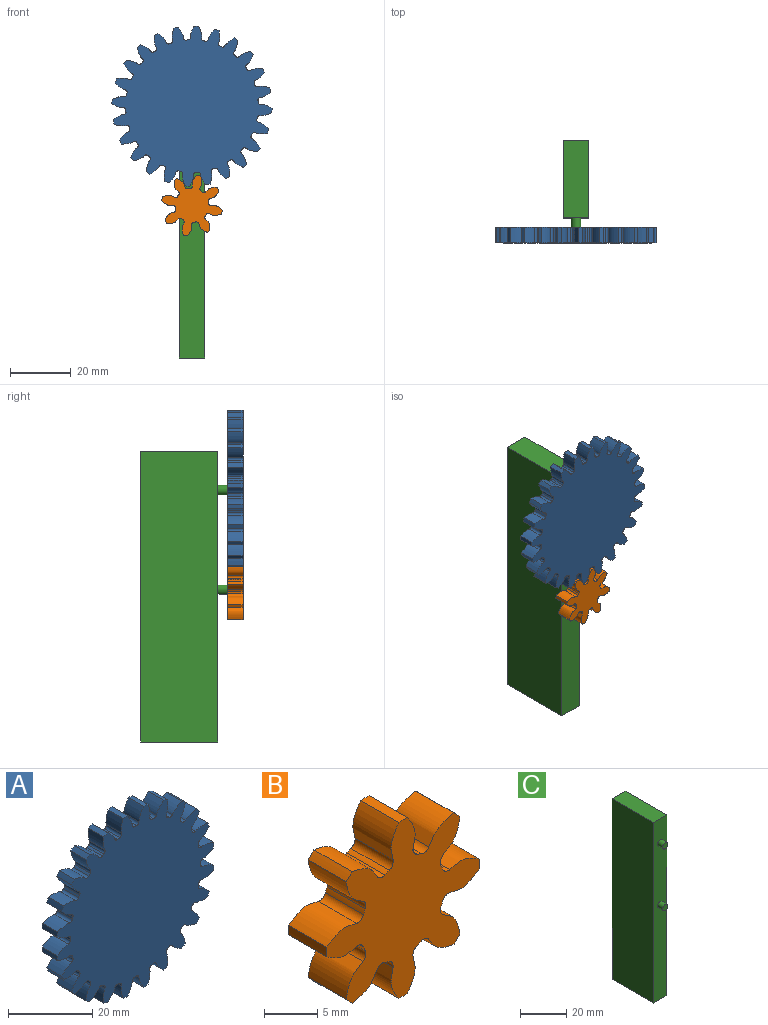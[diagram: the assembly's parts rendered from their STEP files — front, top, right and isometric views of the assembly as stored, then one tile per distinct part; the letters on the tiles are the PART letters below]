
ASSEMBLY  parts=3 mates=2
PART A: 146 faces, bbox 52.6x5.1x52.6 mm
  f0: cylinder r=26.42mm len=5.08mm, axis (0,1,0), area 7.4mm2, adj f23,f25,f121,f143
  f1: cylinder r=26.42mm len=5.08mm, axis (0,1,0), area 7.4mm2, adj f23,f25,f138,f141
  f2: cylinder r=26.42mm len=5.08mm, axis (0,1,0), area 7.4mm2, adj f23,f25,f126,f133
  f3: cylinder r=26.42mm len=5.08mm, axis (0,1,0), area 7.4mm2, adj f23,f25,f128,f136
  f4: cylinder r=26.42mm len=5.08mm, axis (0,1,0), area 7.4mm2, adj f23,f25,f116,f123
  f5: cylinder r=26.42mm len=5.08mm, axis (0,1,0), area 7.4mm2, adj f23,f25,f106,f118
  f6: cylinder r=26.42mm len=5.08mm, axis (0,1,0), area 7.4mm2, adj f23,f25,f101,f113
  f7: cylinder r=26.42mm len=5.08mm, axis (0,1,0), area 7.4mm2, adj f23,f25,f108,f111
  f8: cylinder r=26.42mm len=5.08mm, axis (0,1,0), area 7.4mm2, adj f23,f25,f96,f103
  f9: cylinder r=26.42mm len=5.08mm, axis (0,1,0), area 7.4mm2, adj f23,f25,f91,f98
  f10: cylinder r=26.42mm len=5.08mm, axis (0,1,0), area 7.4mm2, adj f23,f25,f86,f93
  f11: cylinder r=26.42mm len=5.08mm, axis (0,1,0), area 7.4mm2, adj f23,f25,f71,f88
  f12: cylinder r=26.42mm len=5.08mm, axis (0,1,0), area 7.4mm2, adj f23,f25,f26,f83
  f13: cylinder r=26.42mm len=5.08mm, axis (0,1,0), area 7.4mm2, adj f23,f25,f78,f81
  f14: cylinder r=26.42mm len=5.08mm, axis (0,1,0), area 7.4mm2, adj f23,f25,f66,f73
  f15: cylinder r=26.42mm len=5.08mm, axis (0,1,0), area 7.4mm2, adj f23,f25,f68,f76
  f16: cylinder r=26.42mm len=5.08mm, axis (0,1,0), area 7.4mm2, adj f23,f25,f51,f63
  f17: cylinder r=26.42mm len=5.08mm, axis (0,1,0), area 7.4mm2, adj f23,f25,f46,f58
  f18: cylinder r=26.42mm len=5.08mm, axis (0,1,0), area 7.4mm2, adj f23,f25,f53,f56
  f19: cylinder r=26.42mm len=5.08mm, axis (0,1,0), area 7.4mm2, adj f23,f25,f41,f48
  f20: cylinder r=26.42mm len=5.08mm, axis (0,1,0), area 7.4mm2, adj f23,f25,f36,f43
  f21: cylinder r=26.42mm len=5.08mm, axis (0,1,0), area 7.4mm2, adj f23,f25,f31,f38
  f22: cylinder r=26.42mm len=5.08mm, axis (0,1,0), area 7.4mm2, adj f23,f25,f33,f131
  f23: plane 52.56x52.56mm, normal (0,-1,0), area 1838.6mm2, adj f0,f1,f2,f3,f4,f5,f6,f7
  f24: cylinder r=26.42mm len=5.08mm, axis (0,1,0), area 7.4mm2, adj f23,f25,f28,f61
  f25: plane 52.56x52.56mm, normal (0,1,0), area 1838.6mm2, adj f0,f1,f2,f3,f4,f5,f6,f7
  f26: extruded ~5.08x3.7mm, area 20.7mm2, adj f12,f23,f25,f29
  f27: cylinder r=21.84mm len=5.08mm, axis (0,1,0), area 3.6mm2, adj f23,f25,f29,f30
  f28: extruded ~5.08x3.7mm, area 20.7mm2, adj f23,f24,f25,f30
  f29: cylinder r=0.78mm len=5.08mm, axis (0,1,0), area 6.1mm2, adj f23,f25,f26,f27
  f30: cylinder r=0.78mm len=5.08mm, axis (0,1,0), area 6.1mm2, adj f23,f25,f27,f28
  f31: extruded ~5.08x3.98mm, area 20.7mm2, adj f21,f23,f25,f34
  f32: cylinder r=21.84mm len=5.08mm, axis (0,1,0), area 3.6mm2, adj f23,f25,f34,f35
  f33: extruded ~5.08x3.16mm, area 20.7mm2, adj f22,f23,f25,f35
  f34: cylinder r=0.78mm len=5.08mm, axis (0,1,0), area 6.1mm2, adj f23,f25,f31,f32
  f35: cylinder r=0.78mm len=5.08mm, axis (0,1,0), area 6.1mm2, adj f23,f25,f32,f33
  f36: extruded ~5.08x3.7mm, area 20.7mm2, adj f20,f23,f25,f39
  f37: cylinder r=21.84mm len=5.08mm, axis (0,1,0), area 3.6mm2, adj f23,f25,f39,f40
  f38: extruded ~5.08x3.7mm, area 20.7mm2, adj f21,f23,f25,f40
  f39: cylinder r=0.78mm len=5.08mm, axis (0,1,0), area 6.1mm2, adj f23,f25,f36,f37
  f40: cylinder r=0.78mm len=5.08mm, axis (0,1,0), area 6.1mm2, adj f23,f25,f37,f38
  f41: extruded ~5.08x3.16mm, area 20.7mm2, adj f19,f23,f25,f44
  f42: cylinder r=21.84mm len=5.08mm, axis (0,1,0), area 3.6mm2, adj f23,f25,f44,f45
  f43: extruded ~5.08x3.98mm, area 20.7mm2, adj f20,f23,f25,f45
  f44: cylinder r=0.78mm len=5.08mm, axis (0,1,0), area 6.1mm2, adj f23,f25,f41,f42
  f45: cylinder r=0.78mm len=5.08mm, axis (0,1,0), area 6.1mm2, adj f23,f25,f42,f43
  f46: extruded ~5.08x3.22mm, area 20.7mm2, adj f17,f23,f25,f49
  f47: cylinder r=21.84mm len=5.08mm, axis (0,1,0), area 3.6mm2, adj f23,f25,f49,f50
  f48: extruded ~5.08x4mm, area 20.7mm2, adj f19,f23,f25,f50
  f49: cylinder r=0.78mm len=5.08mm, axis (0,1,0), area 6.1mm2, adj f23,f25,f46,f47
  f50: cylinder r=0.78mm len=5.08mm, axis (0,1,0), area 6.1mm2, adj f23,f25,f47,f48
  f51: extruded ~5.08x4mm, area 20.7mm2, adj f16,f23,f25,f54
  f52: cylinder r=21.84mm len=5.08mm, axis (0,1,0), area 3.6mm2, adj f23,f25,f54,f55
  f53: extruded ~5.08x3.22mm, area 20.7mm2, adj f18,f23,f25,f55
  f54: cylinder r=0.78mm len=5.08mm, axis (0,1,0), area 6.1mm2, adj f23,f25,f51,f52
  f55: cylinder r=0.78mm len=5.08mm, axis (0,1,0), area 6.1mm2, adj f23,f25,f52,f53
  f56: extruded ~5.08x3.74mm, area 20.7mm2, adj f18,f23,f25,f59
  f57: cylinder r=21.84mm len=5.08mm, axis (0,1,0), area 3.6mm2, adj f23,f25,f59,f60
  f58: extruded ~5.08x3.74mm, area 20.7mm2, adj f17,f23,f25,f60
  f59: cylinder r=0.78mm len=5.08mm, axis (0,1,0), area 6.1mm2, adj f23,f25,f56,f57
  f60: cylinder r=0.78mm len=5.08mm, axis (0,1,0), area 6.1mm2, adj f23,f25,f57,f58
  f61: extruded ~5.08x3.98mm, area 20.7mm2, adj f23,f24,f25,f64
  f62: cylinder r=21.84mm len=5.08mm, axis (0,1,0), area 3.6mm2, adj f23,f25,f64,f65
  f63: extruded ~5.08x3.16mm, area 20.7mm2, adj f16,f23,f25,f65
  f64: cylinder r=0.78mm len=5.08mm, axis (0,1,0), area 6.1mm2, adj f23,f25,f61,f62
  f65: cylinder r=0.78mm len=5.08mm, axis (0,1,0), area 6.1mm2, adj f23,f25,f62,f63
  f66: extruded ~5.08x3.74mm, area 20.7mm2, adj f14,f23,f25,f69
  f67: cylinder r=21.84mm len=5.08mm, axis (0,1,0), area 3.6mm2, adj f23,f25,f69,f70
  f68: extruded ~5.08x3.74mm, area 20.7mm2, adj f15,f23,f25,f70
  f69: cylinder r=0.78mm len=5.08mm, axis (0,1,0), area 6.1mm2, adj f23,f25,f66,f67
  f70: cylinder r=0.78mm len=5.08mm, axis (0,1,0), area 6.1mm2, adj f23,f25,f67,f68
  f71: extruded ~5.08x4mm, area 20.7mm2, adj f11,f23,f25,f74
  f72: cylinder r=21.84mm len=5.08mm, axis (0,1,0), area 3.6mm2, adj f23,f25,f74,f75
  f73: extruded ~5.08x3.22mm, area 20.7mm2, adj f14,f23,f25,f75
  f74: cylinder r=0.78mm len=5.08mm, axis (0,1,0), area 6.1mm2, adj f23,f25,f71,f72
  f75: cylinder r=0.78mm len=5.08mm, axis (0,1,0), area 6.1mm2, adj f23,f25,f72,f73
  f76: extruded ~5.08x3.22mm, area 20.7mm2, adj f15,f23,f25,f79
  f77: cylinder r=21.84mm len=5.08mm, axis (0,1,0), area 3.6mm2, adj f23,f25,f79,f80
  f78: extruded ~5.08x4mm, area 20.7mm2, adj f13,f23,f25,f80
  f79: cylinder r=0.78mm len=5.08mm, axis (0,1,0), area 6.1mm2, adj f23,f25,f76,f77
  f80: cylinder r=0.78mm len=5.08mm, axis (0,1,0), area 6.1mm2, adj f23,f25,f77,f78
  f81: extruded ~5.08x3.16mm, area 20.7mm2, adj f13,f23,f25,f84
  f82: cylinder r=21.84mm len=5.08mm, axis (0,1,0), area 3.6mm2, adj f23,f25,f84,f85
  f83: extruded ~5.08x3.98mm, area 20.7mm2, adj f12,f23,f25,f85
  f84: cylinder r=0.78mm len=5.08mm, axis (0,1,0), area 6.1mm2, adj f23,f25,f81,f82
  f85: cylinder r=0.78mm len=5.08mm, axis (0,1,0), area 6.1mm2, adj f23,f25,f82,f83
  f86: extruded ~5.08x3.98mm, area 20.7mm2, adj f10,f23,f25,f89
  f87: cylinder r=21.84mm len=5.08mm, axis (0,1,0), area 3.6mm2, adj f23,f25,f89,f90
  f88: extruded ~5.08x3.16mm, area 20.7mm2, adj f11,f23,f25,f90
  f89: cylinder r=0.78mm len=5.08mm, axis (0,1,0), area 6.1mm2, adj f23,f25,f86,f87
  f90: cylinder r=0.78mm len=5.08mm, axis (0,1,0), area 6.1mm2, adj f23,f25,f87,f88
  f91: extruded ~5.08x3.7mm, area 20.7mm2, adj f9,f23,f25,f94
  f92: cylinder r=21.84mm len=5.08mm, axis (0,1,0), area 3.6mm2, adj f23,f25,f94,f95
  f93: extruded ~5.08x3.7mm, area 20.7mm2, adj f10,f23,f25,f95
  f94: cylinder r=0.78mm len=5.08mm, axis (0,1,0), area 6.1mm2, adj f23,f25,f91,f92
  f95: cylinder r=0.78mm len=5.08mm, axis (0,1,0), area 6.1mm2, adj f23,f25,f92,f93
  f96: extruded ~5.08x3.16mm, area 20.7mm2, adj f8,f23,f25,f99
  f97: cylinder r=21.84mm len=5.08mm, axis (0,1,0), area 3.6mm2, adj f23,f25,f99,f100
  f98: extruded ~5.08x3.98mm, area 20.7mm2, adj f9,f23,f25,f100
  f99: cylinder r=0.78mm len=5.08mm, axis (0,1,0), area 6.1mm2, adj f23,f25,f96,f97
  f100: cylinder r=0.78mm len=5.08mm, axis (0,1,0), area 6.1mm2, adj f23,f25,f97,f98
  f101: extruded ~5.08x3.22mm, area 20.7mm2, adj f6,f23,f25,f104
  f102: cylinder r=21.84mm len=5.08mm, axis (0,1,0), area 3.6mm2, adj f23,f25,f104,f105
  f103: extruded ~5.08x4mm, area 20.7mm2, adj f8,f23,f25,f105
  f104: cylinder r=0.78mm len=5.08mm, axis (0,1,0), area 6.1mm2, adj f23,f25,f101,f102
  f105: cylinder r=0.78mm len=5.08mm, axis (0,1,0), area 6.1mm2, adj f23,f25,f102,f103
  f106: extruded ~5.08x4mm, area 20.7mm2, adj f5,f23,f25,f109
  f107: cylinder r=21.84mm len=5.08mm, axis (0,1,0), area 3.6mm2, adj f23,f25,f109,f110
  f108: extruded ~5.08x3.22mm, area 20.7mm2, adj f7,f23,f25,f110
  f109: cylinder r=0.78mm len=5.08mm, axis (0,1,0), area 6.1mm2, adj f23,f25,f106,f107
  f110: cylinder r=0.78mm len=5.08mm, axis (0,1,0), area 6.1mm2, adj f23,f25,f107,f108
  f111: extruded ~5.08x3.74mm, area 20.7mm2, adj f7,f23,f25,f114
  f112: cylinder r=21.84mm len=5.08mm, axis (0,1,0), area 3.6mm2, adj f23,f25,f114,f115
  f113: extruded ~5.08x3.74mm, area 20.7mm2, adj f6,f23,f25,f115
  f114: cylinder r=0.78mm len=5.08mm, axis (0,1,0), area 6.1mm2, adj f23,f25,f111,f112
  f115: cylinder r=0.78mm len=5.08mm, axis (0,1,0), area 6.1mm2, adj f23,f25,f112,f113
  f116: extruded ~5.08x3.98mm, area 20.7mm2, adj f4,f23,f25,f119
  f117: cylinder r=21.84mm len=5.08mm, axis (0,1,0), area 3.6mm2, adj f23,f25,f119,f120
  f118: extruded ~5.08x3.16mm, area 20.7mm2, adj f5,f23,f25,f120
  f119: cylinder r=0.78mm len=5.08mm, axis (0,1,0), area 6.1mm2, adj f23,f25,f116,f117
  f120: cylinder r=0.78mm len=5.08mm, axis (0,1,0), area 6.1mm2, adj f23,f25,f117,f118
  f121: extruded ~5.08x3.7mm, area 20.7mm2, adj f0,f23,f25,f124
  f122: cylinder r=21.84mm len=5.08mm, axis (0,1,0), area 3.6mm2, adj f23,f25,f124,f125
  f123: extruded ~5.08x3.7mm, area 20.7mm2, adj f4,f23,f25,f125
  f124: cylinder r=0.78mm len=5.08mm, axis (0,1,0), area 6.1mm2, adj f23,f25,f121,f122
  f125: cylinder r=0.78mm len=5.08mm, axis (0,1,0), area 6.1mm2, adj f23,f25,f122,f123
  f126: extruded ~5.08x3.74mm, area 20.7mm2, adj f2,f23,f25,f129
  f127: cylinder r=21.84mm len=5.08mm, axis (0,1,0), area 3.6mm2, adj f23,f25,f129,f130
  f128: extruded ~5.08x3.74mm, area 20.7mm2, adj f3,f23,f25,f130
  f129: cylinder r=0.78mm len=5.08mm, axis (0,1,0), area 6.1mm2, adj f23,f25,f126,f127
  f130: cylinder r=0.78mm len=5.08mm, axis (0,1,0), area 6.1mm2, adj f23,f25,f127,f128
  f131: extruded ~5.08x4mm, area 20.7mm2, adj f22,f23,f25,f134
  f132: cylinder r=21.84mm len=5.08mm, axis (0,1,0), area 3.6mm2, adj f23,f25,f134,f135
  f133: extruded ~5.08x3.22mm, area 20.7mm2, adj f2,f23,f25,f135
  f134: cylinder r=0.78mm len=5.08mm, axis (0,1,0), area 6.1mm2, adj f23,f25,f131,f132
  f135: cylinder r=0.78mm len=5.08mm, axis (0,1,0), area 6.1mm2, adj f23,f25,f132,f133
  f136: extruded ~5.08x3.22mm, area 20.7mm2, adj f3,f23,f25,f139
  f137: cylinder r=21.84mm len=5.08mm, axis (0,1,0), area 3.6mm2, adj f23,f25,f139,f140
  f138: extruded ~5.08x4mm, area 20.7mm2, adj f1,f23,f25,f140
  f139: cylinder r=0.78mm len=5.08mm, axis (0,1,0), area 6.1mm2, adj f23,f25,f136,f137
  f140: cylinder r=0.78mm len=5.08mm, axis (0,1,0), area 6.1mm2, adj f23,f25,f137,f138
  f141: extruded ~5.08x3.16mm, area 20.7mm2, adj f1,f23,f25,f144
  f142: cylinder r=21.84mm len=5.08mm, axis (0,1,0), area 3.6mm2, adj f23,f25,f144,f145
  f143: extruded ~5.08x3.98mm, area 20.7mm2, adj f0,f23,f25,f145
  f144: cylinder r=0.78mm len=5.08mm, axis (0,1,0), area 6.1mm2, adj f23,f25,f141,f142
  f145: cylinder r=0.78mm len=5.08mm, axis (0,1,0), area 6.1mm2, adj f23,f25,f142,f143
PART B: 50 faces, bbox 20.4x5.1x20.4 mm
  f0: cylinder r=10.16mm len=5.08mm, axis (0,1,0), area 5.6mm2, adj f7,f9,f40,f47
  f1: cylinder r=10.16mm len=5.08mm, axis (0,1,0), area 5.6mm2, adj f7,f9,f35,f42
  f2: cylinder r=10.16mm len=5.08mm, axis (0,1,0), area 5.6mm2, adj f7,f9,f30,f37
  f3: cylinder r=10.16mm len=5.08mm, axis (0,1,0), area 5.6mm2, adj f7,f9,f25,f32
  f4: cylinder r=10.16mm len=5.08mm, axis (0,1,0), area 5.6mm2, adj f7,f9,f20,f27
  f5: cylinder r=10.16mm len=5.08mm, axis (0,1,0), area 5.6mm2, adj f7,f9,f15,f22
  f6: cylinder r=10.16mm len=5.08mm, axis (0,1,0), area 5.6mm2, adj f7,f9,f10,f17
  f7: plane 20.39x20.39mm, normal (0,-1,0), area 197mm2, adj f0,f1,f2,f3,f4,f5,f6,f8
  f8: cylinder r=10.16mm len=5.08mm, axis (0,1,0), area 5.6mm2, adj f7,f9,f12,f45
  f9: plane 20.39x20.39mm, normal (0,1,0), area 197mm2, adj f0,f1,f2,f3,f4,f5,f6,f8
  f10: extruded ~5.08x3.34mm, area 21.3mm2, adj f6,f7,f9,f13
  f11: cylinder r=5.59mm len=5.08mm, axis (0,1,0), area 3mm2, adj f7,f9,f13,f14
  f12: extruded ~5.08x3.93mm, area 21.3mm2, adj f7,f8,f9,f14
  f13: cylinder r=0.82mm len=5.08mm, axis (0,1,0), area 6mm2, adj f7,f9,f10,f11
  f14: cylinder r=0.82mm len=5.08mm, axis (0,1,0), area 6mm2, adj f7,f9,f11,f12
  f15: extruded ~5.08x3.93mm, area 21.3mm2, adj f5,f7,f9,f18
  f16: cylinder r=5.59mm len=5.08mm, axis (0,1,0), area 3mm2, adj f7,f9,f18,f19
  f17: extruded ~5.08x3.34mm, area 21.3mm2, adj f6,f7,f9,f19
  f18: cylinder r=0.82mm len=5.08mm, axis (0,1,0), area 6mm2, adj f7,f9,f15,f16
  f19: cylinder r=0.82mm len=5.08mm, axis (0,1,0), area 6mm2, adj f7,f9,f16,f17
  f20: extruded ~5.08x3.34mm, area 21.3mm2, adj f4,f7,f9,f23
  f21: cylinder r=5.59mm len=5.08mm, axis (0,1,0), area 3mm2, adj f7,f9,f23,f24
  f22: extruded ~5.08x3.93mm, area 21.3mm2, adj f5,f7,f9,f24
  f23: cylinder r=0.82mm len=5.08mm, axis (0,1,0), area 6mm2, adj f7,f9,f20,f21
  f24: cylinder r=0.82mm len=5.08mm, axis (0,1,0), area 6mm2, adj f7,f9,f21,f22
  f25: extruded ~5.08x3.93mm, area 21.3mm2, adj f3,f7,f9,f28
  f26: cylinder r=5.59mm len=5.08mm, axis (0,1,0), area 3mm2, adj f7,f9,f28,f29
  f27: extruded ~5.08x3.34mm, area 21.3mm2, adj f4,f7,f9,f29
  f28: cylinder r=0.82mm len=5.08mm, axis (0,1,0), area 6mm2, adj f7,f9,f25,f26
  f29: cylinder r=0.82mm len=5.08mm, axis (0,1,0), area 6mm2, adj f7,f9,f26,f27
  f30: extruded ~5.08x3.34mm, area 21.3mm2, adj f2,f7,f9,f33
  f31: cylinder r=5.59mm len=5.08mm, axis (0,1,0), area 3mm2, adj f7,f9,f33,f34
  f32: extruded ~5.08x3.93mm, area 21.3mm2, adj f3,f7,f9,f34
  f33: cylinder r=0.82mm len=5.08mm, axis (0,1,0), area 6mm2, adj f7,f9,f30,f31
  f34: cylinder r=0.82mm len=5.08mm, axis (0,1,0), area 6mm2, adj f7,f9,f31,f32
  f35: extruded ~5.08x3.93mm, area 21.3mm2, adj f1,f7,f9,f38
  f36: cylinder r=5.59mm len=5.08mm, axis (0,1,0), area 3mm2, adj f7,f9,f38,f39
  f37: extruded ~5.08x3.34mm, area 21.3mm2, adj f2,f7,f9,f39
  f38: cylinder r=0.82mm len=5.08mm, axis (0,1,0), area 6mm2, adj f7,f9,f35,f36
  f39: cylinder r=0.82mm len=5.08mm, axis (0,1,0), area 6mm2, adj f7,f9,f36,f37
  f40: extruded ~5.08x3.34mm, area 21.3mm2, adj f0,f7,f9,f43
  f41: cylinder r=5.59mm len=5.08mm, axis (0,1,0), area 3mm2, adj f7,f9,f43,f44
  f42: extruded ~5.08x3.93mm, area 21.3mm2, adj f1,f7,f9,f44
  f43: cylinder r=0.82mm len=5.08mm, axis (0,1,0), area 6mm2, adj f7,f9,f40,f41
  f44: cylinder r=0.82mm len=5.08mm, axis (0,1,0), area 6mm2, adj f7,f9,f41,f42
  f45: extruded ~5.08x3.93mm, area 21.3mm2, adj f7,f8,f9,f48
  f46: cylinder r=5.59mm len=5.08mm, axis (0,1,0), area 3mm2, adj f7,f9,f48,f49
  f47: extruded ~5.08x3.34mm, area 21.3mm2, adj f0,f7,f9,f49
  f48: cylinder r=0.82mm len=5.08mm, axis (0,1,0), area 6mm2, adj f7,f9,f45,f46
  f49: cylinder r=0.82mm len=5.08mm, axis (0,1,0), area 6mm2, adj f7,f9,f46,f47
PART C: 10 faces, bbox 8.3x28.6x95.8 mm
  f0: plane 25.4x8.26mm, normal (0,0,1), area 209.8mm2, adj f1,f3,f4,f5
  f1: plane 95.77x25.4mm, normal (-1,0,0), area 2432.5mm2, adj f0,f2,f4,f5
  f2: plane 25.4x8.26mm, normal (0,0,-1), area 209.8mm2, adj f1,f3,f4,f5
  f3: plane 95.77x25.4mm, normal (1,0,0), area 2432.5mm2, adj f0,f2,f4,f5
  f4: plane 95.77x8.26mm, normal (0,-1,0), area 775.3mm2, adj f0,f1,f2,f3,f6,f8
  f5: plane 95.77x8.26mm, normal (0,1,0), area 791.1mm2, adj f0,f1,f2,f3
  f6: cylinder r=1.59mm len=3.18mm, axis (0,1,0), area 31.7mm2, adj f4,f7
  f7: plane 3.18x3.18mm, normal (0,-1,0), area 7.9mm2, adj f6
  f8: cylinder r=1.59mm len=3.18mm, axis (0,1,0), area 31.7mm2, adj f4,f9
  f9: plane 3.18x3.18mm, normal (0,-1,0), area 7.9mm2, adj f8
PLACE A rot(axis=(0,-1,0),49.2deg) t=(39.47,-14.29,36.8)mm
PLACE B rot(axis=(0,1,0),147.6deg) t=(39.47,-14.29,4.04)mm
PLACE C t=(106.63,14.29,12.19)mm fixed
MATE revolute A.f0 <-> C.f6  axis (0,1,0) through (39.47,-14.29,36.8)mm
MATE revolute B.f0 <-> C.f8  axis (0,1,0) through (39.47,-14.29,4.04)mm
